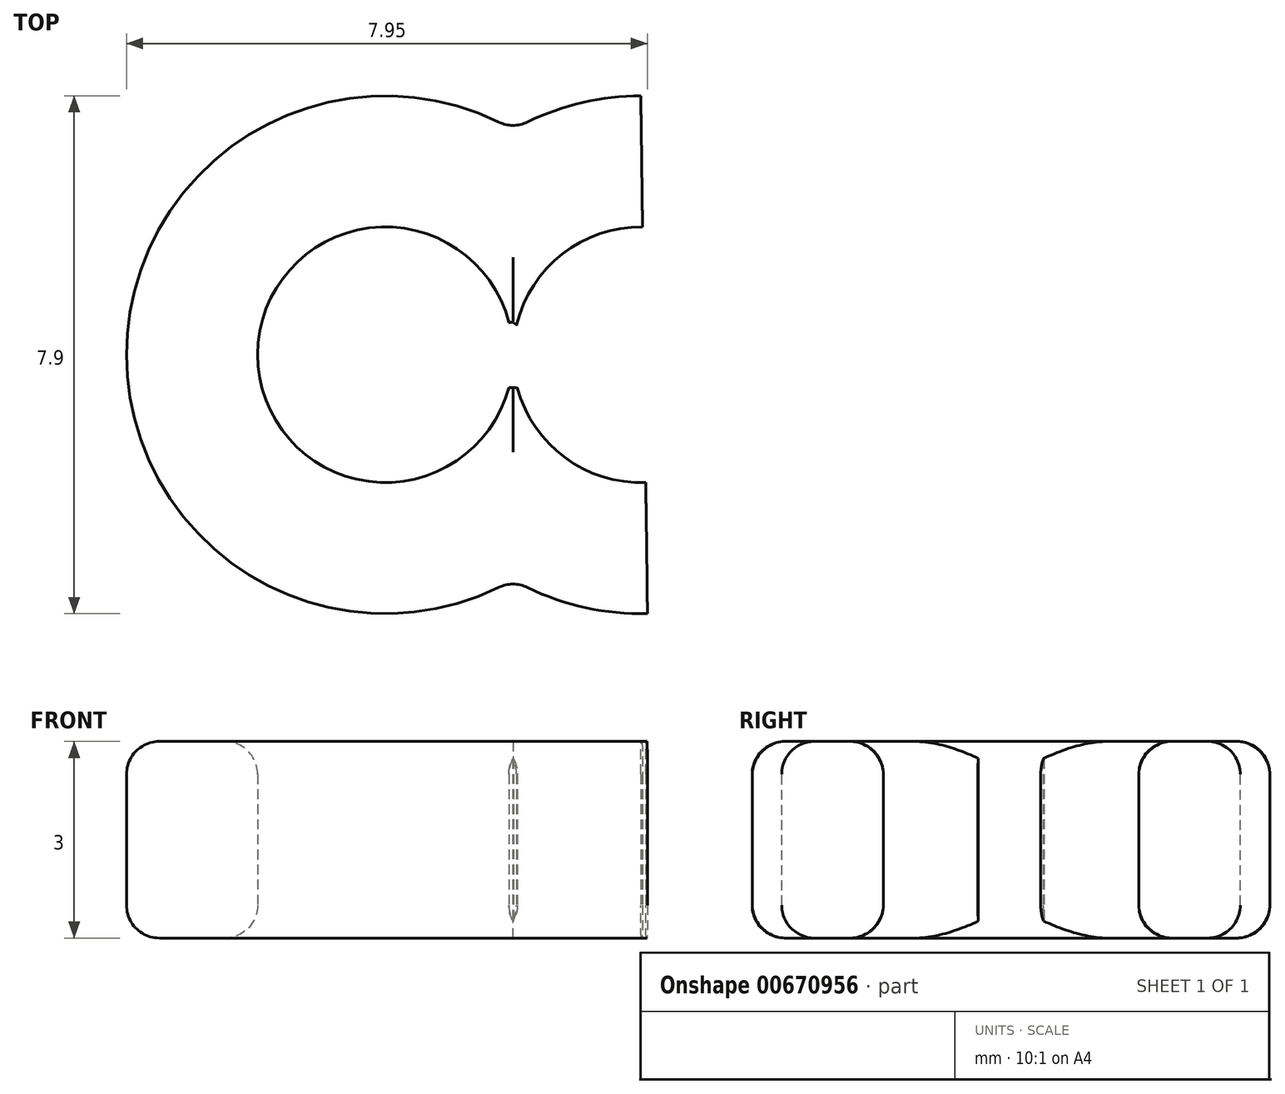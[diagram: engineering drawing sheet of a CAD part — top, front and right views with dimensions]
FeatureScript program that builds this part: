
annotation { "Feature Type Name" : "Feature", "Feature Type Description" : "" }
export const myFeature = defineFeature(function(context is Context, id is Id, definition is map)
    precondition{}
    {
        {
            var Q0;
            Q0=qCreatedBy(makeId("Top.planeOp"),FACE);
            var sketch = newSketch(context, id + "F0", { "sketchPlane" : qUnion([Q0])});
            skCircle(sketch, "E0", {"center": v(0, 0) * mm, "radius": 1.95 * mm});
            skCircle(sketch, "E1", {"center": v(3.9, 0) * mm, "radius": 1.95 * mm});
            skLineSegment(sketch, "E2", {"start": v(3.9, 1.95) * mm, "end": v(3.9, -1.95) * mm});
            skCircle(sketch, "E3.0", {"center": v(0, 0) * mm, "radius": 3.95 * mm});
            skCircle(sketch, "E4.0", {"center": v(3.9, 0) * mm, "radius": 3.95 * mm});
            skLineSegment(sketch, "E5", {"start": v(0, 3.95) * mm, "end": v(3.9, 3.95) * mm});
            skLineSegment(sketch, "E6", {"start": v(3.9, 3.95) * mm, "end": v(4, -3.95) * mm});
            skLineSegment(sketch, "E7", {"start": v(4, -3.95) * mm, "end": v(0, -4.05) * mm});
            skLineSegment(sketch, "E8", {"start": v(0, -4.05) * mm, "end": v(0, 3.95) * mm});
            skLineSegment(sketch, "E9", {"start": v(3.9, 0) * mm, "end": v(3.94, 1) * mm});
            skLineSegment(sketch, "E10", {"start": v(3.94, 1) * mm, "end": v(3.96, -1) * mm});
            skLineSegment(sketch, "E11", {"start": v(3.96, -1) * mm, "end": v(7.72, -1) * mm});
            skLineSegment(sketch, "E12", {"start": v(7.72, -1) * mm, "end": v(7.7, 1.1) * mm});
            skLineSegment(sketch, "E13", {"start": v(7.7, 1.1) * mm, "end": v(3.94, 1) * mm});
            skLineSegment(sketch, "E14", {"start": v(0, 0) * mm, "end": v(3.9, 0) * mm});
            skLineSegment(sketch, "E15", {"start": v(1.95, 0) * mm, "end": v(1.94, 0.5) * mm});
            skLineSegment(sketch, "E16", {"start": v(1.94, 0.5) * mm, "end": v(1.96, -0.5) * mm});
            skLineSegment(sketch, "E17", {"start": v(1.96, -0.5) * mm, "end": v(1.67, -0.5) * mm});
            skLineSegment(sketch, "E18", {"start": v(1.67, -0.5) * mm, "end": v(1.66, 0.45) * mm});
            skLineSegment(sketch, "E19", {"start": v(1.66, 0.45) * mm, "end": v(1.94, 0.5) * mm});
            skLineSegment(sketch, "E20", {"start": v(1.94, 0.5) * mm, "end": v(2.16, 0.33) * mm});
            skLineSegment(sketch, "E21", {"start": v(2.16, 0.33) * mm, "end": v(2.16, -0.52) * mm});
            skLineSegment(sketch, "E22", {"start": v(2.16, -0.52) * mm, "end": v(1.96, -0.5) * mm});
            skSolve(sketch);
        }
        {
            var Q0;
            {var subQ0=sQuery(id+"F0.wireOp",EDGE,"E8");var subQ1=sQuery(id+"F0.wireOp",EDGE,"E0");var subQ2=makeQuery(id+"F0.imprint","INTERSECT",VERTEX,{"disambiguationData":[OD(0.0)],"derivedFrom":[subQ1,subQ0]});Q0=makeQuery(id+"F0.imprint","IMPRINT",FACE,{"disambiguationData":[TD([[makeQuery(id+"F0.imprint","IMPRINT",EDGE,{"disambiguationData":[TD([[subQ2,-1.0]])],"derivedFrom":subQ1}),-1.0]])]});}
            var Q1;
            {var subQ0=sQuery(id+"F0.wireOp",EDGE,"E4.0");var subQ1=sQuery(id+"F0.wireOp",EDGE,"E0");var subQ2=makeQuery(id+"F0.imprint","INTERSECT",VERTEX,{"disambiguationData":[OD(0.0)],"derivedFrom":[subQ1,subQ0]});Q1=makeQuery(id+"F0.imprint","IMPRINT",FACE,{"disambiguationData":[TD([[makeQuery(id+"F0.imprint","IMPRINT",EDGE,{"disambiguationData":[TD([[subQ2,-1.0]])],"derivedFrom":subQ1}),-1.0]])]});}
            var Q2;
            {var subQ6=sQuery(id+"F0.wireOp",EDGE,"E19");var subQ8=sQuery(id+"F0.wireOp",EDGE,"E0");var subQ9=makeQuery(id+"F0.imprint","INTERSECT",VERTEX,{"derivedFrom":[subQ8,subQ6]});Q2=makeQuery(id+"F0.imprint","IMPRINT",FACE,{"disambiguationData":[TD([[makeQuery(id+"F0.imprint","IMPRINT",EDGE,{"disambiguationData":[TD([[subQ9,-1.0]])],"derivedFrom":subQ8}),-1.0]])]});}
            var Q3;
            {var subQ5=sQuery(id+"F0.wireOp",EDGE,"E1");var subQ7=makeQuery(id+"F0.imprint","INTERSECT",VERTEX,{"disambiguationData":[OD(0.0)],"derivedFrom":[subQ5,sQuery(id+"F0.wireOp",EDGE,"E2")]});Q3=makeQuery(id+"F0.imprint","IMPRINT",FACE,{"disambiguationData":[TD([[makeQuery(id+"F0.imprint","IMPRINT",EDGE,{"disambiguationData":[TD([[subQ7,1.0]])],"derivedFrom":subQ5}),-1.0]])]});}
            var Q4;
            {var subQ0=sQuery(id+"F0.wireOp",EDGE,"E6");var subQ1=sQuery(id+"F0.wireOp",EDGE,"E1");var subQ2=makeQuery(id+"F0.imprint","INTERSECT",VERTEX,{"disambiguationData":[OD(0.0)],"derivedFrom":[subQ1,subQ0]});Q4=makeQuery(id+"F0.imprint","IMPRINT",FACE,{"disambiguationData":[TD([[makeQuery(id+"F0.imprint","IMPRINT",EDGE,{"disambiguationData":[TD([[subQ2,1.0]])],"derivedFrom":subQ1}),-1.0]])]});}
            var Q5;
            {var subQ0=sQuery(id+"F0.wireOp",EDGE,"E6");var subQ1=sQuery(id+"F0.wireOp",EDGE,"E1");var subQ2=makeQuery(id+"F0.imprint","INTERSECT",VERTEX,{"disambiguationData":[OD(1.0)],"derivedFrom":[subQ1,subQ0]});Q5=makeQuery(id+"F0.imprint","IMPRINT",FACE,{"disambiguationData":[TD([[makeQuery(id+"F0.imprint","IMPRINT",EDGE,{"disambiguationData":[TD([[subQ2,-1.0]])],"derivedFrom":subQ1}),-1.0]])]});}
            var Q6;
            {var subQ0=sQuery(id+"F0.wireOp",EDGE,"E1");var subQ1=makeQuery(id+"F0.imprint","INTERSECT",VERTEX,{"disambiguationData":[OD(1.0)],"derivedFrom":[subQ0,sQuery(id+"F0.wireOp",EDGE,"E2")]});Q6=makeQuery(id+"F0.imprint","IMPRINT",FACE,{"disambiguationData":[TD([[makeQuery(id+"F0.imprint","IMPRINT",EDGE,{"disambiguationData":[TD([[subQ1,1.0]])],"derivedFrom":subQ0}),-1.0]])]});}
            var Q7;
            {var subQ0=sQuery(id+"F0.wireOp",EDGE,"E8");var subQ1=sQuery(id+"F0.wireOp",EDGE,"E0");var subQ2=makeQuery(id+"F0.imprint","INTERSECT",VERTEX,{"disambiguationData":[OD(1.0)],"derivedFrom":[subQ1,subQ0]});Q7=makeQuery(id+"F0.imprint","IMPRINT",FACE,{"disambiguationData":[TD([[makeQuery(id+"F0.imprint","IMPRINT",EDGE,{"disambiguationData":[TD([[subQ2,-1.0]])],"derivedFrom":subQ1}),-1.0]])]});}
            var Q8;
            {var subQ3=sQuery(id+"F0.wireOp",EDGE,"E4.0");var subQ5=sQuery(id+"F0.wireOp",EDGE,"E0");var subQ6=makeQuery(id+"F0.imprint","INTERSECT",VERTEX,{"disambiguationData":[OD(1.0)],"derivedFrom":[subQ5,subQ3]});Q8=makeQuery(id+"F0.imprint","IMPRINT",FACE,{"disambiguationData":[TD([[makeQuery(id+"F0.imprint","IMPRINT",EDGE,{"disambiguationData":[TD([[subQ6,-1.0]])],"derivedFrom":subQ5}),-1.0]])]});}
            extrude(context, id + "F1", {"entities" : qUnion([Q0, Q1, Q2, Q3, Q4, Q5, Q6, Q7, Q8]), "depth" : 3 * mm, "offsetDistance" : 25 * mm});
        }
        {
            var Q0;
            {var subQ0=sQuery(id+"F0.wireOp",EDGE,"E4.0");var subQ1=makeQuery(id+"F0.imprint","INTERSECT",VERTEX,{"derivedFrom":[subQ0,sQuery(id+"F0.wireOp",EDGE,"E5"),sQuery(id+"F0.wireOp",EDGE,"E6")]});Q0=makeQuery(id+"F1.opExtrude","CAP_EDGE",EDGE,{"disambiguationData":[OSD([subQ0]),TDD([makeQuery(id+"F0.imprint","IMPRINT",EDGE,{"disambiguationData":[TD([[subQ1,1.0]])],"derivedFrom":subQ0}),makeQuery(id+"F0.imprint","IMPRINT",EDGE,{"disambiguationData":[TD([[makeQuery(id+"F0.imprint","INTERSECT",VERTEX,{"disambiguationData":[OD(0.0)],"derivedFrom":[sQuery(id+"F0.wireOp",EDGE,"E3.0"),subQ0]}),1.0]])],"derivedFrom":subQ0})])],"isStart":false});}
            var Q1;
            {var subQ0=sQuery(id+"F0.wireOp",EDGE,"E1");var subQ1=makeQuery(id+"F0.imprint","INTERSECT",VERTEX,{"disambiguationData":[OD(0.0)],"derivedFrom":[subQ0,sQuery(id+"F0.wireOp",EDGE,"E3.0")]});var subQ2=makeQuery(id+"F0.imprint","INTERSECT",VERTEX,{"disambiguationData":[OD(0.0)],"derivedFrom":[subQ0,sQuery(id+"F0.wireOp",EDGE,"E2")]});var subQ3=makeQuery(id+"F0.imprint","INTERSECT",VERTEX,{"disambiguationData":[OD(0.0)],"derivedFrom":[subQ0,sQuery(id+"F0.wireOp",EDGE,"E6")]});Q1=makeQuery(id+"F1.opExtrude","CAP_EDGE",EDGE,{"disambiguationData":[OSD([subQ0]),TDD([makeQuery(id+"F0.imprint","IMPRINT",EDGE,{"disambiguationData":[TD([[subQ3,1.0]])],"derivedFrom":subQ0}),makeQuery(id+"F0.imprint","IMPRINT",EDGE,{"disambiguationData":[TD([[subQ2,1.0]])],"derivedFrom":subQ0}),makeQuery(id+"F0.imprint","IMPRINT",EDGE,{"disambiguationData":[TD([[subQ2,-1.0]])],"derivedFrom":subQ0}),makeQuery(id+"F0.imprint","IMPRINT",EDGE,{"disambiguationData":[TD([[subQ1,-1.0]])],"derivedFrom":subQ0})])],"isStart":false});}
            var Q2;
            {var subQ0=sQuery(id+"F0.wireOp",EDGE,"E1");var subQ1=makeQuery(id+"F0.imprint","INTERSECT",VERTEX,{"disambiguationData":[OD(1.0)],"derivedFrom":[subQ0,sQuery(id+"F0.wireOp",EDGE,"E6")]});var subQ2=makeQuery(id+"F0.imprint","INTERSECT",VERTEX,{"disambiguationData":[OD(1.0)],"derivedFrom":[subQ0,sQuery(id+"F0.wireOp",EDGE,"E2")]});Q2=makeQuery(id+"F1.opExtrude","CAP_EDGE",EDGE,{"disambiguationData":[OSD([subQ0]),TDD([makeQuery(id+"F0.imprint","IMPRINT",EDGE,{"disambiguationData":[TD([[makeQuery(id+"F0.imprint","INTERSECT",VERTEX,{"derivedFrom":[subQ0,sQuery(id+"F0.wireOp",EDGE,"E22")]}),-1.0]])],"derivedFrom":subQ0}),makeQuery(id+"F0.imprint","IMPRINT",EDGE,{"disambiguationData":[TD([[subQ2,1.0]])],"derivedFrom":subQ0}),makeQuery(id+"F0.imprint","IMPRINT",EDGE,{"disambiguationData":[TD([[subQ2,-1.0]])],"derivedFrom":subQ0}),makeQuery(id+"F0.imprint","IMPRINT",EDGE,{"disambiguationData":[TD([[subQ1,-1.0]])],"derivedFrom":subQ0})])],"isStart":false});}
            var Q3;
            {var subQ0=sQuery(id+"F0.wireOp",EDGE,"E1");var subQ1=makeQuery(id+"F0.imprint","INTERSECT",VERTEX,{"disambiguationData":[OD(1.0)],"derivedFrom":[subQ0,sQuery(id+"F0.wireOp",EDGE,"E6")]});var subQ2=makeQuery(id+"F0.imprint","INTERSECT",VERTEX,{"disambiguationData":[OD(1.0)],"derivedFrom":[subQ0,sQuery(id+"F0.wireOp",EDGE,"E2")]});Q3=makeQuery(id+"F1.opExtrude","CAP_EDGE",EDGE,{"disambiguationData":[OSD([subQ0]),TDD([makeQuery(id+"F0.imprint","IMPRINT",EDGE,{"disambiguationData":[TD([[makeQuery(id+"F0.imprint","INTERSECT",VERTEX,{"derivedFrom":[subQ0,sQuery(id+"F0.wireOp",EDGE,"E22")]}),-1.0]])],"derivedFrom":subQ0}),makeQuery(id+"F0.imprint","IMPRINT",EDGE,{"disambiguationData":[TD([[subQ2,1.0]])],"derivedFrom":subQ0}),makeQuery(id+"F0.imprint","IMPRINT",EDGE,{"disambiguationData":[TD([[subQ2,-1.0]])],"derivedFrom":subQ0}),makeQuery(id+"F0.imprint","IMPRINT",EDGE,{"disambiguationData":[TD([[subQ1,-1.0]])],"derivedFrom":subQ0})])],"isStart":true});}
            var Q4;
            Q4=makeQuery(id+"F1.opExtrude","CAP_EDGE",EDGE,{"disambiguationData":[OSD([sQuery(id+"F0.wireOp",EDGE,"E0")])],"isStart":false});
            var Q5;
            Q5=makeQuery(id+"F1.opExtrude","CAP_EDGE",EDGE,{"disambiguationData":[OSD([sQuery(id+"F0.wireOp",EDGE,"E0")])],"isStart":true});
            var Q6;
            {var subQ0=sQuery(id+"F0.wireOp",EDGE,"E4.0");var subQ1=makeQuery(id+"F0.imprint","INTERSECT",VERTEX,{"derivedFrom":[subQ0,sQuery(id+"F0.wireOp",EDGE,"E6"),sQuery(id+"F0.wireOp",EDGE,"E7")]});Q6=makeQuery(id+"F1.opExtrude","CAP_EDGE",EDGE,{"disambiguationData":[OSD([subQ0]),TDD([makeQuery(id+"F0.imprint","IMPRINT",EDGE,{"disambiguationData":[TD([[makeQuery(id+"F0.imprint","INTERSECT",VERTEX,{"disambiguationData":[OD(1.0)],"derivedFrom":[sQuery(id+"F0.wireOp",EDGE,"E3.0"),subQ0]}),-1.0]])],"derivedFrom":subQ0}),makeQuery(id+"F0.imprint","IMPRINT",EDGE,{"disambiguationData":[TD([[subQ1,-1.0]])],"derivedFrom":subQ0})])],"isStart":false});}
            var Q7;
            Q7=makeQuery(id+"F1.opExtrude","CAP_EDGE",EDGE,{"disambiguationData":[OSD([sQuery(id+"F0.wireOp",EDGE,"E3.0")])],"isStart":false});
            var Q8;
            Q8=makeQuery(id+"F1.opExtrude","CAP_EDGE",EDGE,{"disambiguationData":[OSD([sQuery(id+"F0.wireOp",EDGE,"E3.0")])],"isStart":true});
            var Q9;
            {var subQ0=sQuery(id+"F0.wireOp",EDGE,"E4.0");var subQ1=makeQuery(id+"F0.imprint","INTERSECT",VERTEX,{"derivedFrom":[subQ0,sQuery(id+"F0.wireOp",EDGE,"E6"),sQuery(id+"F0.wireOp",EDGE,"E7")]});Q9=makeQuery(id+"F1.opExtrude","CAP_EDGE",EDGE,{"disambiguationData":[OSD([subQ0]),TDD([makeQuery(id+"F0.imprint","IMPRINT",EDGE,{"disambiguationData":[TD([[makeQuery(id+"F0.imprint","INTERSECT",VERTEX,{"disambiguationData":[OD(1.0)],"derivedFrom":[sQuery(id+"F0.wireOp",EDGE,"E3.0"),subQ0]}),-1.0]])],"derivedFrom":subQ0}),makeQuery(id+"F0.imprint","IMPRINT",EDGE,{"disambiguationData":[TD([[subQ1,-1.0]])],"derivedFrom":subQ0})])],"isStart":true});}
            var Q10;
            {var subQ0=sQuery(id+"F0.wireOp",EDGE,"E1");var subQ1=makeQuery(id+"F0.imprint","INTERSECT",VERTEX,{"disambiguationData":[OD(0.0)],"derivedFrom":[subQ0,sQuery(id+"F0.wireOp",EDGE,"E3.0")]});var subQ2=makeQuery(id+"F0.imprint","INTERSECT",VERTEX,{"disambiguationData":[OD(0.0)],"derivedFrom":[subQ0,sQuery(id+"F0.wireOp",EDGE,"E2")]});var subQ3=makeQuery(id+"F0.imprint","INTERSECT",VERTEX,{"disambiguationData":[OD(0.0)],"derivedFrom":[subQ0,sQuery(id+"F0.wireOp",EDGE,"E6")]});Q10=makeQuery(id+"F1.opExtrude","CAP_EDGE",EDGE,{"disambiguationData":[OSD([subQ0]),TDD([makeQuery(id+"F0.imprint","IMPRINT",EDGE,{"disambiguationData":[TD([[subQ3,1.0]])],"derivedFrom":subQ0}),makeQuery(id+"F0.imprint","IMPRINT",EDGE,{"disambiguationData":[TD([[subQ2,1.0]])],"derivedFrom":subQ0}),makeQuery(id+"F0.imprint","IMPRINT",EDGE,{"disambiguationData":[TD([[subQ2,-1.0]])],"derivedFrom":subQ0}),makeQuery(id+"F0.imprint","IMPRINT",EDGE,{"disambiguationData":[TD([[subQ1,-1.0]])],"derivedFrom":subQ0})])],"isStart":true});}
            var Q11;
            {var subQ0=sQuery(id+"F0.wireOp",EDGE,"E4.0");var subQ1=makeQuery(id+"F0.imprint","INTERSECT",VERTEX,{"derivedFrom":[subQ0,sQuery(id+"F0.wireOp",EDGE,"E5"),sQuery(id+"F0.wireOp",EDGE,"E6")]});Q11=makeQuery(id+"F1.opExtrude","CAP_EDGE",EDGE,{"disambiguationData":[OSD([subQ0]),TDD([makeQuery(id+"F0.imprint","IMPRINT",EDGE,{"disambiguationData":[TD([[subQ1,1.0]])],"derivedFrom":subQ0}),makeQuery(id+"F0.imprint","IMPRINT",EDGE,{"disambiguationData":[TD([[makeQuery(id+"F0.imprint","INTERSECT",VERTEX,{"disambiguationData":[OD(0.0)],"derivedFrom":[sQuery(id+"F0.wireOp",EDGE,"E3.0"),subQ0]}),1.0]])],"derivedFrom":subQ0})])],"isStart":true});}
            var Q12;
            Q12=makeQuery(id+"F1.opExtrude","SWEPT_EDGE",EDGE,{"disambiguationData":[OSD([sQuery(id+"F0.wireOp",EDGE,"E4.0"),sQuery(id+"F0.wireOp",EDGE,"E11"),sQuery(id+"F0.wireOp",EDGE,"E12")])]});
            var Q13;
            Q13=makeQuery(id+"F1.opExtrude","SWEPT_EDGE",EDGE,{"disambiguationData":[OSD([sQuery(id+"F0.wireOp",EDGE,"E4.0"),sQuery(id+"F0.wireOp",EDGE,"E12"),sQuery(id+"F0.wireOp",EDGE,"E13")])]});
            fillet(context, id + "F2", {"entities" : qUnion([Q0, Q1, Q2, Q3, Q4, Q5, Q6, Q7, Q8, Q9, Q10, Q11, Q12, Q13]), "radius" : 0.5 * mm, "tangentPropagation" : true, "allowEdgeOverflow" : false});
        }
    });
